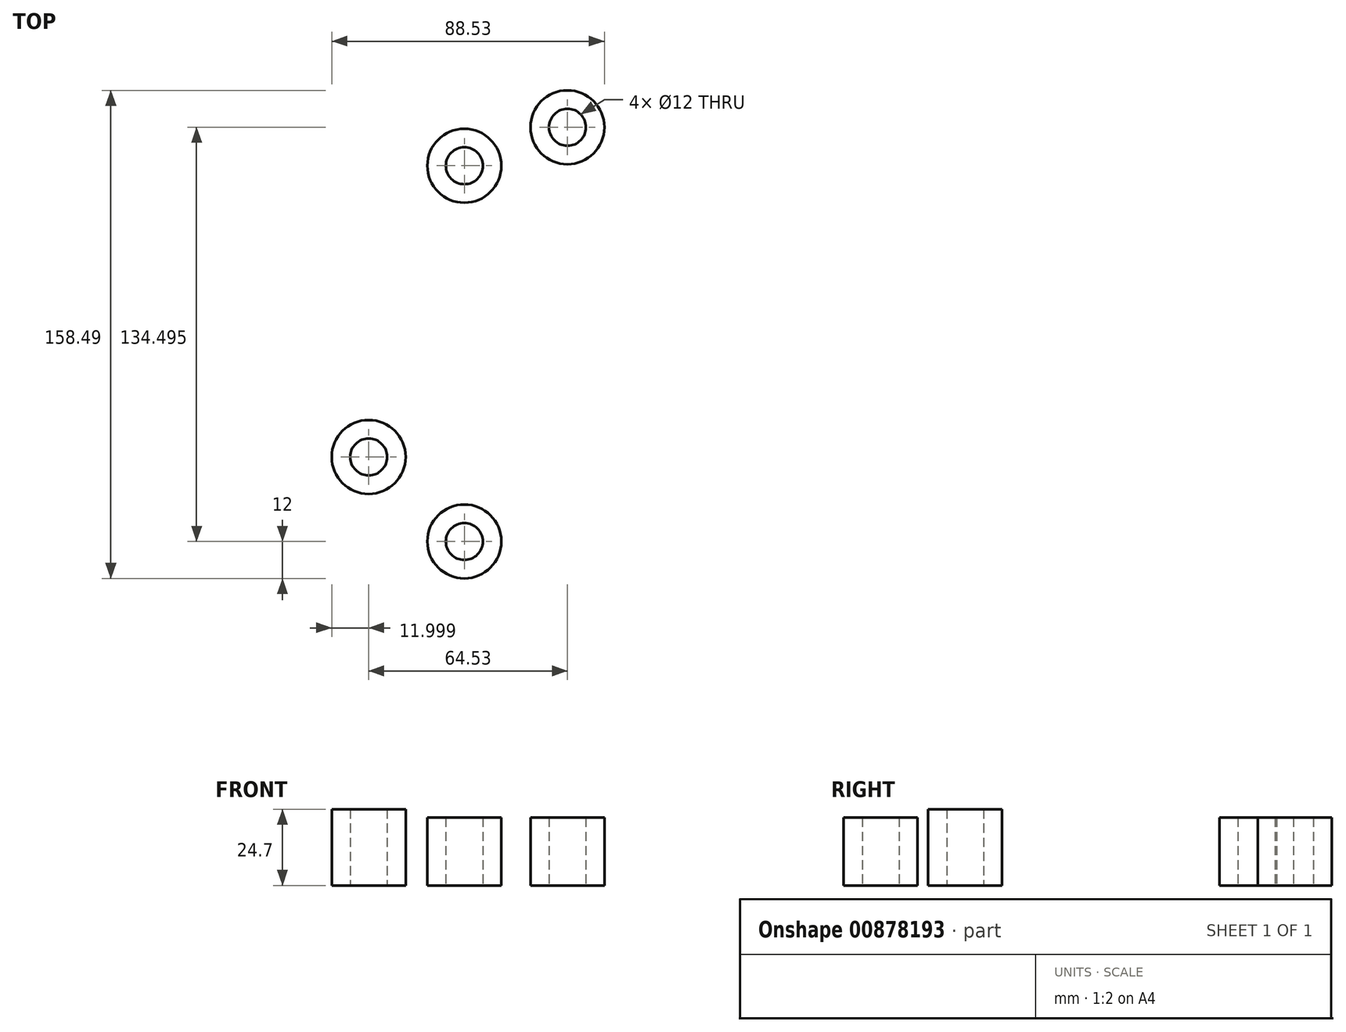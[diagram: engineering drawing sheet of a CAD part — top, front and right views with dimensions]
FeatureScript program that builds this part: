
annotation { "Feature Type Name" : "Feature", "Feature Type Description" : "" }
export const myFeature = defineFeature(function(context is Context, id is Id, definition is map)
    precondition{}
    {
        {
            var Q0;
            Q0=qCreatedBy(makeId("Top.planeOp"),FACE);
            var sketch = newSketch(context, id + "F0", { "sketchPlane" : qUnion([Q0])});
            skCircle(sketch, "E0", {"center": v(0, 0) * mm, "radius": 73.5 * mm, "construction": true});
            skCircle(sketch, "E1", {"center": v(0, 0) * mm, "radius": 70 * mm, "construction": true});
            skCircle(sketch, "E2", {"center": v(-34.34, 61) * mm, "radius": 6 * mm});
            skCircle(sketch, "E3", {"center": v(-34.34, -61) * mm, "radius": 6 * mm});
            skCircle(sketch, "E4", {"center": v(-65.4, -33.56) * mm, "radius": 6 * mm});
            skCircle(sketch, "E5", {"center": v(-0.86, 73.5) * mm, "radius": 6 * mm});
            skLineSegment(sketch, "E6", {"start": v(-0.86, 73.5) * mm, "end": v(-65.4, -33.56) * mm, "construction": true});
            skLineSegment(sketch, "E7", {"start": v(-34.34, 61) * mm, "end": v(-34.34, -61) * mm, "construction": true});
            skCircle(sketch, "E8", {"center": v(-65.4, -33.56) * mm, "radius": 12 * mm});
            skCircle(sketch, "E9", {"center": v(-34.34, -61) * mm, "radius": 12 * mm});
            skCircle(sketch, "E10", {"center": v(-0.86, 73.5) * mm, "radius": 12 * mm});
            skCircle(sketch, "E11", {"center": v(-34.34, 61) * mm, "radius": 12 * mm});
            skLineSegment(sketch, "E12", {"start": v(-34.34, -61) * mm, "end": v(-22.34, -61) * mm});
            skLineSegment(sketch, "E13", {"start": v(-22.34, -61) * mm, "end": v(-22.34, 51.12) * mm});
            skPoint(sketch, "E14.start.orphan", {"position": v(-22.34, 61) * mm});
            skLineSegment(sketch, "E15", {"start": v(-33.13, 19.97) * mm, "end": v(-56.25, 33.9) * mm, "construction": true});
            skCircle(sketch, "E16", {"center": v(-82.03, -13.76) * mm, "radius": 2.5 * mm});
            skCircle(sketch, "E17", {"center": v(-28.88, 75.63) * mm, "radius": 2.5 * mm});
            skLineSegment(sketch, "E18", {"start": v(-82.03, -13.76) * mm, "end": v(-28.88, 75.63) * mm, "construction": true});
            skSolve(sketch);
        }
        {
            var Q0;
            Q0=makeQuery(id+"F0.imprint","IMPRINT",FACE,{"disambiguationData":[TD([[makeQuery(id+"F0.imprint","IMPRINT",EDGE,{"derivedFrom":sQuery(id+"F0.wireOp",EDGE,"E2")}),-1.0]])]});
            var Q1;
            Q1=makeQuery(id+"F0.imprint","IMPRINT",FACE,{"disambiguationData":[TD([[makeQuery(id+"F0.imprint","IMPRINT",EDGE,{"derivedFrom":sQuery(id+"F0.wireOp",EDGE,"E3")}),-1.0]])]});
            var Q2;
            {var subQ0=sQuery(id+"F0.wireOp",EDGE,"uvAYMqGV-DIzJ-fmoX-Jquh-CrT9dVzAXWpi");Q2=makeQuery(id+"F0.imprint","IMPRINT",FACE,{"disambiguationData":[TD([[makeQuery(id+"F0.imprint","IMPRINT",EDGE,{"derivedFrom":subQ0}),1.0]])]});}
            var Q3;
            Q3=makeQuery(id+"F0.imprint","IMPRINT",FACE,{"disambiguationData":[TD([[makeQuery(id+"F0.imprint","IMPRINT",EDGE,{"derivedFrom":sQuery(id+"F0.wireOp",EDGE,"E5")}),-1.0]])]});
            var Q4;
            {var subQ0=sQuery(id+"F0.wireOp",EDGE,"5625360e-2d45-4daa-a3da-605d3618f61e.trimOffspring");Q4=makeQuery(id+"F0.imprint","IMPRINT",FACE,{"disambiguationData":[TD([[makeQuery(id+"F0.imprint","IMPRINT",EDGE,{"derivedFrom":subQ0}),1.0]])]});}
            var Q5;
            {var subQ8=sQuery(id+"F0.wireOp",EDGE,"UsUqNIiJ-VfbJ-wgNQ-Aa4I-qdWGud0cX9Ic");Q5=makeQuery(id+"F0.imprint","IMPRINT",FACE,{"disambiguationData":[TD([[makeQuery(id+"F0.imprint","IMPRINT",EDGE,{"derivedFrom":subQ8}),1.0]])]});}
            var Q6;
            {var subQ5=sQuery(id+"F0.wireOp",EDGE,"7202584b-8c20-40f0-bc9d-29dd12e960fb.trimOffspring");Q6=makeQuery(id+"F0.imprint","IMPRINT",FACE,{"disambiguationData":[TD([[makeQuery(id+"F0.imprint","IMPRINT",EDGE,{"derivedFrom":subQ5}),-1.0]])]});}
            extrude(context, id + "F1", {"entities" : qUnion([Q0, Q1, Q2, Q3, Q4, Q5, Q6]), "depth" : 22 * mm, "offsetDistance" : 25 * mm});
        }
        {
            var Q0;
            Q0=makeQuery(id+"F0.imprint","IMPRINT",FACE,{"disambiguationData":[TD([[makeQuery(id+"F0.imprint","IMPRINT",EDGE,{"derivedFrom":sQuery(id+"F0.wireOp",EDGE,"E4")}),-1.0]])]});
            extrude(context, id + "F2", {"entities" : qUnion([Q0]), "operationType" : NewBodyOperationType.ADD, "depth" : 24.7 * mm, "offsetDistance" : 25 * mm});
        }
    });
